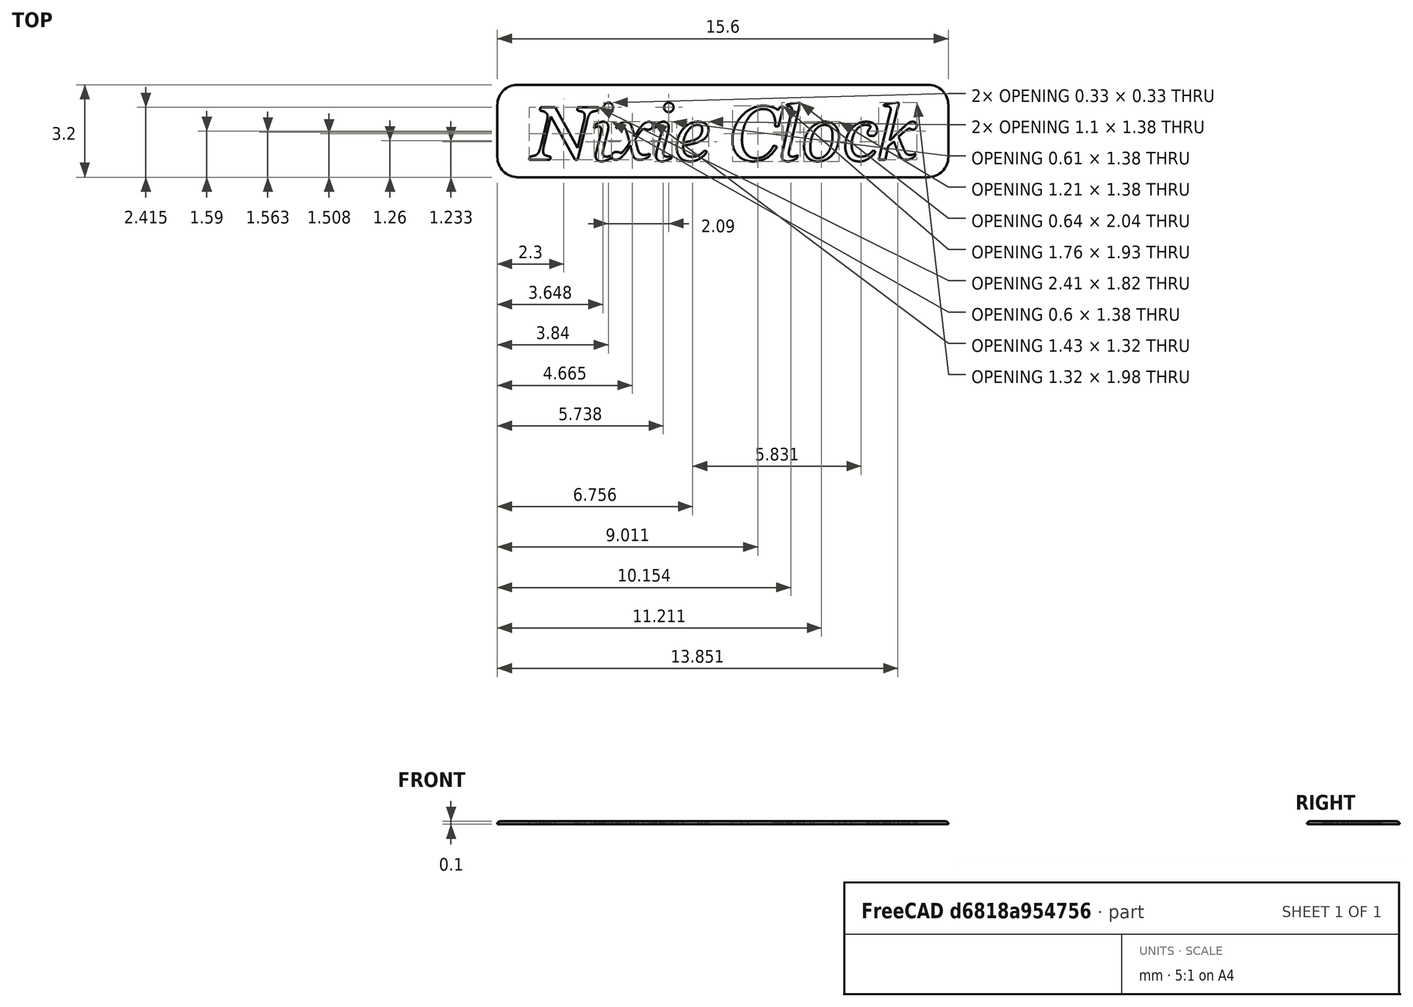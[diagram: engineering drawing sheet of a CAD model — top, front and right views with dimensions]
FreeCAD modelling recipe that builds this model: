
FCSTD DOCUMENT  (FreeCAD 0.16R6712 (Git))
Label: tag
License: All rights reserved
LicenseURL: http://en.wikipedia.org/wiki/All_rights_reserved
objects: Part::Extrusion×2, Part::Part2DObjectPython×1, Sketcher::SketchObject×1, Part::Cut×1, PartDesign::Fillet×1, Mesh::Feature×1
note: 6 computed .brp shape members not serialized (recipe doc carries the construction recipe); baked Part::Feature solids carry a one-line shape summary decoded from their .brp

FEATURE [Part::Part2DObjectPython] ShapeString  # Draft 2D object (typed FeaturePython)
  FontFile = <path>
  Size = 2
  String = Nixie Clock
  Tracking = 0
FEATURE [Part::Extrusion] Extrude
  Base = -> ShapeString
  Dir = (0,0,0.4)
  Placement = pos=(0,0,-0.2) rot=(0,0,1;0rad)
  Solid = true
FEATURE [Sketcher::SketchObject] Sketch
  sketch-geometry (8):
    g0: LineSegment StartX=-0.5 StartY=2.6 StartZ=0 EndX=13.7 EndY=2.6 EndZ=0
    g1: LineSegment StartX=14.4 StartY=1.9 StartZ=0 EndX=14.4 EndY=0.1 EndZ=0
    g2: LineSegment StartX=13.7 StartY=-0.6 StartZ=0 EndX=-0.5 EndY=-0.6 EndZ=0
    g3: LineSegment StartX=-1.2 StartY=0.1 StartZ=0 EndX=-1.2 EndY=1.9 EndZ=0
    g4: ArcOfCircle CenterX=-0.5 CenterY=1.9 CenterZ=0 NormalX=0 NormalY=0 NormalZ=1 Radius=0.7 StartAngle=1.5708 EndAngle=3.14159
    g5: ArcOfCircle CenterX=-0.5 CenterY=0.1 CenterZ=0 NormalX=0 NormalY=0 NormalZ=1 Radius=0.7 StartAngle=3.14159 EndAngle=4.71239
    g6: ArcOfCircle CenterX=13.7 CenterY=0.1 CenterZ=0 NormalX=0 NormalY=0 NormalZ=1 Radius=0.7 StartAngle=4.71239 EndAngle=6.28319
    g7: ArcOfCircle CenterX=13.7 CenterY=1.9 CenterZ=0 NormalX=0 NormalY=0 NormalZ=1 Radius=0.7 StartAngle=0 EndAngle=1.5708
  constraints (20):
    c: Horizontal(g0)
    c: Horizontal(g2)
    c: Vertical(g1)
    c: Vertical(g3)
    c: Tangent(g0,g4) = 1.5708
    c: Tangent(g3,g4) = 1.5708
    c: Tangent(g3,g5) = 1.5708
    c: Tangent(g2,g5) = 1.5708
    c: Tangent(g2,g6) = 1.5708
    c: Tangent(g1,g6) = 1.5708
    c: Tangent(g1,g7) = 1.5708
    c: Tangent(g0,g7) = 1.5708
    c: Radius(g7) = 0.7
    c: Equal(g7,g4)
    c: Equal(g4,g5)
    c: Equal(g5,g6)
    c: DistanceY(g-1,g2) = -0.6
    c: DistanceX(g-2,g3) = -1.2
    c: Distance(g3,g1) = 15.6
    c: Distance(g2,g0) = 3.2
FEATURE [Part::Extrusion] Extrude001
  Base = -> Sketch
  Dir = (0,0,0.1)
  Solid = true
FEATURE [Part::Cut] Cut
  Base = -> Extrude001
  Tool = -> Extrude
FEATURE [PartDesign::Fillet] Fillet
  Base = -> Cut [Edge10,Edge330,Edge4,Edge7,Edge329,Edge332,Edge333,Edge331]
  Radius = 0.09
FEATURE [Mesh::Feature] Mesh  label="Fillet (Meshed)"
  Placement = pos=(-6.6,-9,7.3) rot=(0,0,1;0rad)
note: 1 file-system path scrubbed to <path> (originals preserved in the JSON sidecar)
